# Revit family: 641-22-DN900
name_source: partatom
category: Pipe Accessories
units: mm (PartAtom-declared; Revit-internal decimal feet)

## family parameters
Always vertical = Yes
Cut with Voids When Loaded = No
Part Type = Valve - Breaks Into
Round Connector Dimension = Use Diameter
Shared = No
Work Plane-Based = No

## types (1)
- DN900_PN16
    Body_T = 35 mm  [stored 0.114829 ft]
    Bore_R = 450 mm  [stored 1.47638 ft]
    DN = 900 mm  [stored 2.95276 ft]
    DN900_PN16 = 641_0900_22101008
    Default Elevation = 0 mm  [stored 0 ft]
    Description_ = Recoil Valve With Proximity switch DN900 PN16
    FL_T = 47 mm
    Fillet = 25 mm  [stored 0.082021 ft]
    L = 1300 mm  [stored 4.26509 ft]
    Middle_FL_R = 850 mm  [stored 2.78871 ft]
    Middle_FL_T = 55 mm  [stored 0.180446 ft]
    OD = 563 mm
    Raised_R = 501 mm
    Raised_dis = 5 mm  [stored 0.0164042 ft]
    Ring_R = 15 mm  [stored 0.0492126 ft]
    Side1 = 750 mm  [stored 2.46063 ft]
    URL_Product_pages = https://www.avkvalves.com
    edge_dis = 525 mm
    hook_H = 650 mm  [stored 2.13255 ft]
    hook_dim = 200 mm  [stored 0.656168 ft]
    hook_dim1 = 45 mm  [stored 0.147638 ft]
    hook_dim2 = 40 mm  [stored 0.131234 ft]
    logo = 25 mm  [stored 0.082021 ft]
    middle_FL = 892 mm  [stored 2.92651 ft]

note: [stored X ft] marks values corroborated as IEEE doubles in the binary element streams (Revit-internal decimal feet)

## geometry (parser evidence)
native form markers: Sweep x7
no freeform markers — native parametric forms only
